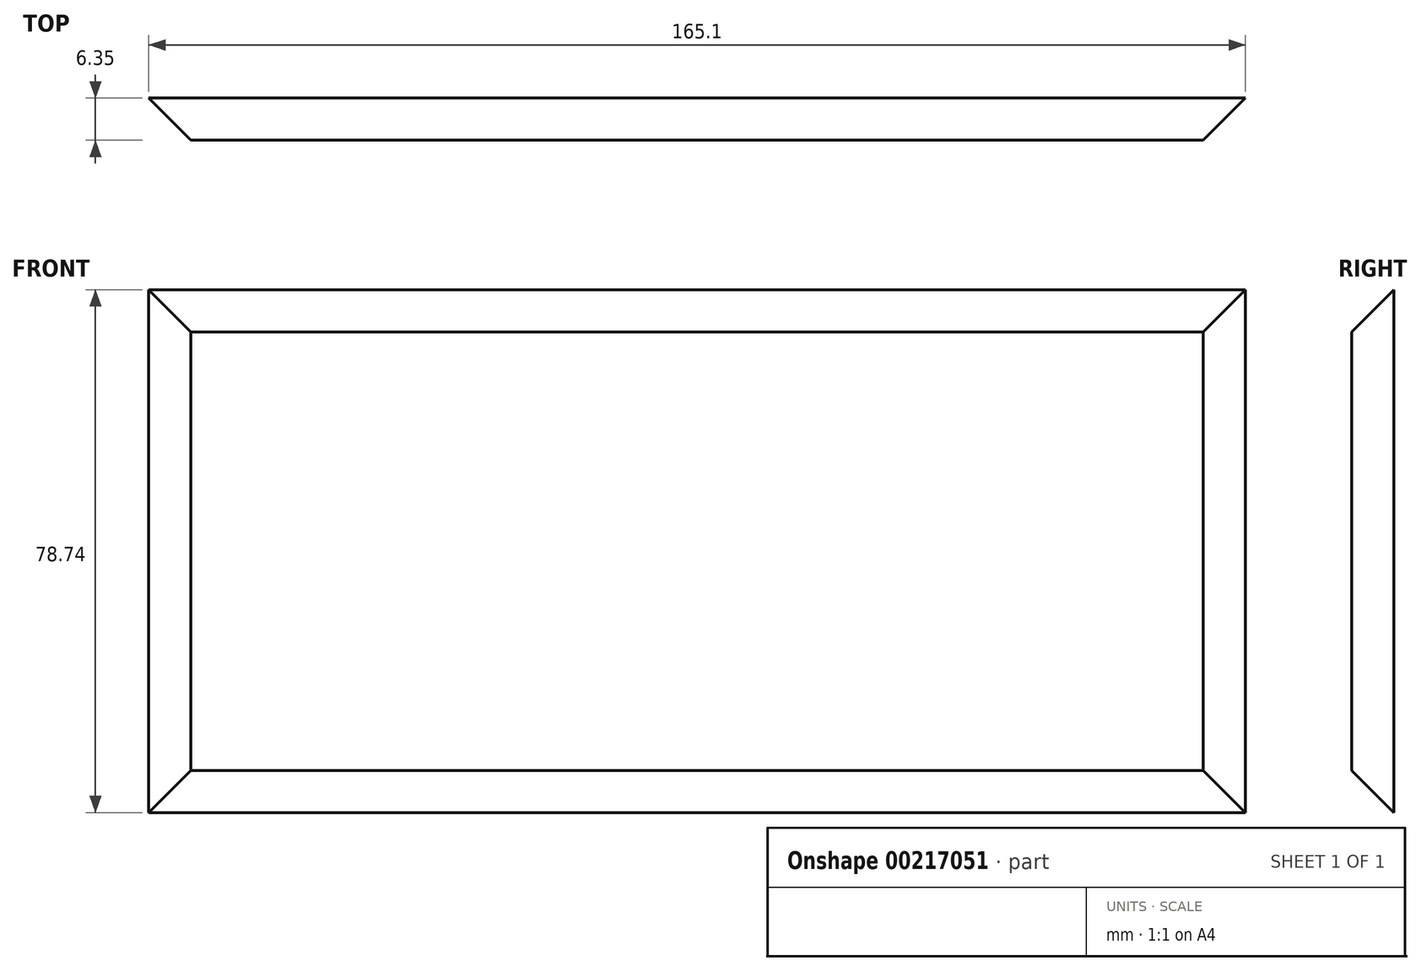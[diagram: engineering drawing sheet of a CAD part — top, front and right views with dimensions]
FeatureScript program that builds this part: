
annotation { "Feature Type Name" : "Feature", "Feature Type Description" : "" }
export const myFeature = defineFeature(function(context is Context, id is Id, definition is map)
    precondition{}
    {
        {
            var Q0;
            Q0=qCreatedBy(makeId("Front.planeOp"),FACE);
            var sketch = newSketch(context, id + "F0", { "sketchPlane" : qUnion([Q0])});
            skPoint(sketch, "E0.middle", {"position": v(0, 0) * mm});
            skLineSegment(sketch, "E1.0", {"start": v(82.55, 39.37) * mm, "end": v(-82.55, 39.37) * mm});
            skLineSegment(sketch, "E1.1", {"start": v(82.55, -39.37) * mm, "end": v(82.55, 39.37) * mm});
            skLineSegment(sketch, "E1.2", {"start": v(82.55, -39.37) * mm, "end": v(-82.55, -39.37) * mm});
            skLineSegment(sketch, "E1.3", {"start": v(-82.55, -39.37) * mm, "end": v(-82.55, 39.37) * mm});
            skPoint(sketch, "E0.left.end.orphan", {"position": v(88.9, 45.72) * mm});
            skPoint(sketch, "E0.bottom.start.orphan", {"position": v(88.9, -45.72) * mm});
            skPoint(sketch, "E0.right.end.orphan", {"position": v(-88.9, 45.72) * mm});
            skPoint(sketch, "E0.right.start.orphan", {"position": v(-88.9, -45.72) * mm});
            skSolve(sketch);
        }
        {
            var Q0;
            Q0 = qSketchRegion(id + "F0", true);
            extrude(context, id + "F1", {"entities" : qUnion([Q0]), "depth" : 6.35 * mm});
        }
        {
            var Q0;
            Q0=makeQuery(id+"F1.opExtrude","CAP_FACE",FACE,{"disambiguationData":[OSD([sQuery(id+"F0.wireOp",EDGE,"E1.0"),sQuery(id+"F0.wireOp",EDGE,"E1.1"),sQuery(id+"F0.wireOp",EDGE,"E1.2"),sQuery(id+"F0.wireOp",EDGE,"E1.3")])],"isStart":false});
            chamfer(context, id + "F2", {"entities" : qUnion([Q0]), "width" : 6.35 * mm, "tangentPropagation" : true});
        }
    });
